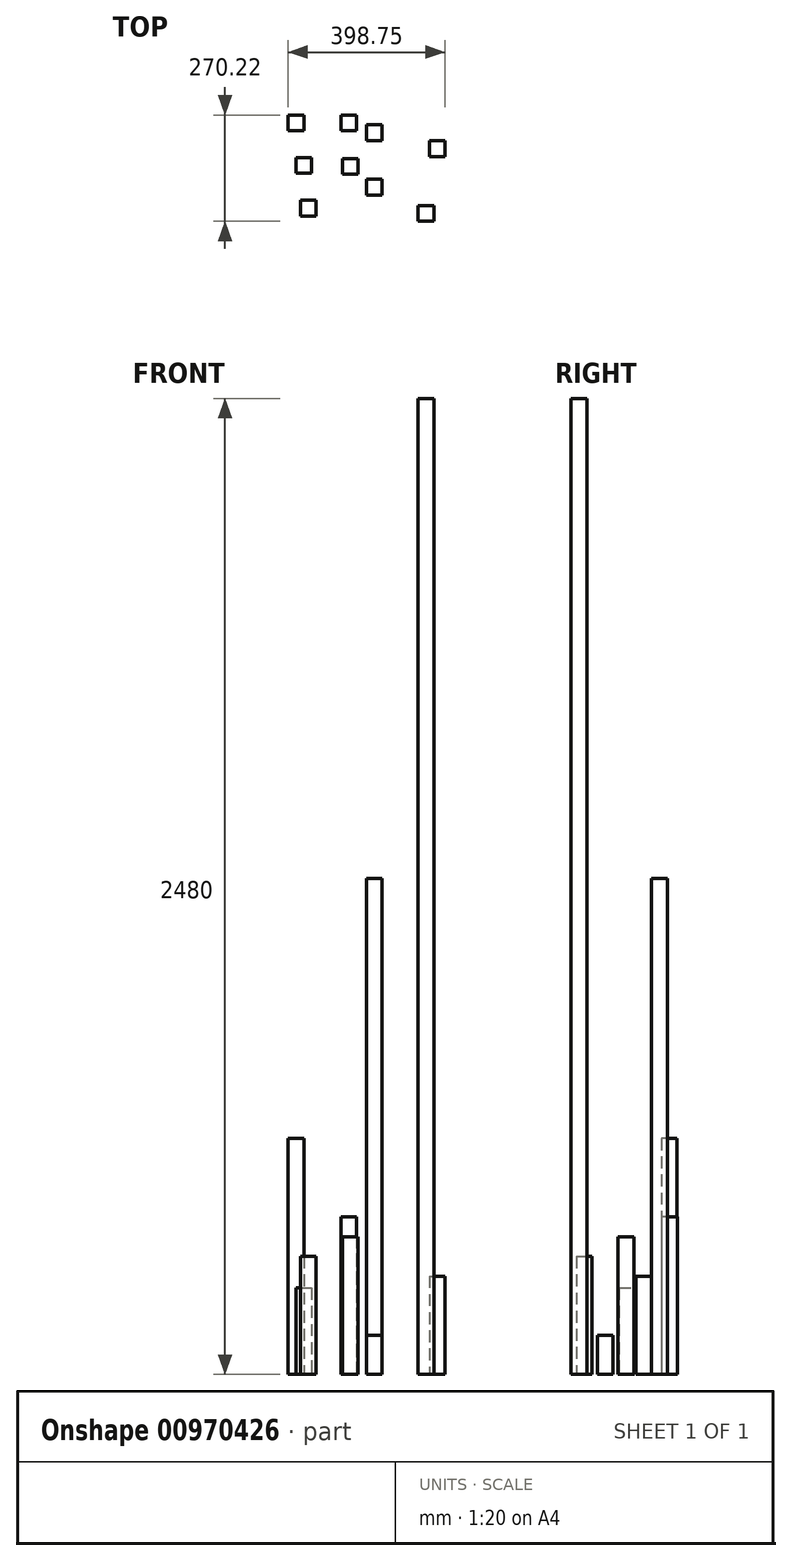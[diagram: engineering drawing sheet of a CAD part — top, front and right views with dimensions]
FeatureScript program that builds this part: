
annotation { "Feature Type Name" : "Feature", "Feature Type Description" : "" }
export const myFeature = defineFeature(function(context is Context, id is Id, definition is map)
    precondition{}
    {
        {
            var Q0;
            Q0=qCreatedBy(makeId("Top.planeOp"),FACE);
            var sketch = newSketch(context, id + "F0", { "sketchPlane" : qUnion([Q0])});
            skLineSegment(sketch, "E0.bottom", {"start": v(0, 0) * mm, "end": v(40, 0) * mm});
            skLineSegment(sketch, "E0.top", {"start": v(0, 40) * mm, "end": v(40, 40) * mm});
            skLineSegment(sketch, "E0.left", {"start": v(0, 0) * mm, "end": v(0, 40) * mm});
            skLineSegment(sketch, "E0.right", {"start": v(40, 0) * mm, "end": v(40, 40) * mm});
            skSolve(sketch);
        }
        {
            var Q0;
            Q0 = qSketchRegion(id + "F0", true);
            extrude(context, id + "F1", {"entities" : qUnion([Q0]), "depth" : 1260 * mm, "offsetDistance" : 25 * mm});
        }
        {
            var Q0;
            Q0=qCreatedBy(makeId("Top.planeOp"),FACE);
            var sketch = newSketch(context, id + "F2", { "sketchPlane" : qUnion([Q0])});
            skLineSegment(sketch, "E1.bottom", {"start": v(-178.75, -83.16) * mm, "end": v(-138.75, -83.16) * mm});
            skLineSegment(sketch, "E1.top", {"start": v(-178.75, -43.16) * mm, "end": v(-138.75, -43.16) * mm});
            skLineSegment(sketch, "E1.left", {"start": v(-178.75, -83.16) * mm, "end": v(-178.75, -43.16) * mm});
            skLineSegment(sketch, "E1.right", {"start": v(-138.75, -83.16) * mm, "end": v(-138.75, -43.16) * mm});
            skSolve(sketch);
        }
        {
            var Q0;
            Q0 = qSketchRegion(id + "F2", true);
            extrude(context, id + "F3", {"entities" : qUnion([Q0]), "depth" : 220 * mm, "offsetDistance" : 25 * mm});
        }
        {
            var Q0;
            Q0=qCreatedBy(makeId("Top.planeOp"),FACE);
            var sketch = newSketch(context, id + "F4", { "sketchPlane" : qUnion([Q0])});
            skLineSegment(sketch, "E2.bottom", {"start": v(159.9, -40.58) * mm, "end": v(199.9, -40.58) * mm});
            skLineSegment(sketch, "E2.top", {"start": v(159.9, -0.58) * mm, "end": v(199.9, -0.58) * mm});
            skLineSegment(sketch, "E2.left", {"start": v(159.9, -40.58) * mm, "end": v(159.9, -0.58) * mm});
            skLineSegment(sketch, "E2.right", {"start": v(199.9, -40.58) * mm, "end": v(199.9, -0.58) * mm});
            skSolve(sketch);
        }
        {
            var Q0;
            Q0=makeQuery(id+"F4.imprint","IMPRINT",FACE,{"disambiguationData":[TD([[makeQuery(id+"F4.imprint","IMPRINT",EDGE,{"derivedFrom":sQuery(id+"F4.wireOp",EDGE,"E2.bottom")}),1.0]])]});
            extrude(context, id + "F5", {"entities" : qUnion([Q0]), "depth" : 250 * mm, "offsetDistance" : 25 * mm});
        }
        {
            var Q0;
            Q0=qCreatedBy(makeId("Top.planeOp"),FACE);
            var sketch = newSketch(context, id + "F6", { "sketchPlane" : qUnion([Q0])});
            skLineSegment(sketch, "E3.bottom", {"start": v(-167.6, -191.22) * mm, "end": v(-127.6, -191.22) * mm});
            skLineSegment(sketch, "E3.top", {"start": v(-167.6, -151.22) * mm, "end": v(-127.6, -151.22) * mm});
            skLineSegment(sketch, "E3.left", {"start": v(-167.6, -191.22) * mm, "end": v(-167.6, -151.22) * mm});
            skLineSegment(sketch, "E3.right", {"start": v(-127.6, -191.22) * mm, "end": v(-127.6, -151.22) * mm});
            skSolve(sketch);
        }
        {
            var Q0;
            Q0 = qSketchRegion(id + "F6", true);
            extrude(context, id + "F7", {"entities" : qUnion([Q0]), "depth" : 300 * mm, "offsetDistance" : 25 * mm});
        }
        {
            var Q0;
            Q0=qCreatedBy(makeId("Top.planeOp"),FACE);
            var sketch = newSketch(context, id + "F8", { "sketchPlane" : qUnion([Q0])});
            skLineSegment(sketch, "E4.bottom", {"start": v(131.45, -205) * mm, "end": v(171.45, -205) * mm});
            skLineSegment(sketch, "E4.top", {"start": v(131.45, -165) * mm, "end": v(171.45, -165) * mm});
            skLineSegment(sketch, "E4.left", {"start": v(131.45, -205) * mm, "end": v(131.45, -165) * mm});
            skLineSegment(sketch, "E4.right", {"start": v(171.45, -205) * mm, "end": v(171.45, -165) * mm});
            skSolve(sketch);
        }
        {
            var Q0;
            Q0=makeQuery(id+"F8.imprint","IMPRINT",FACE,{"disambiguationData":[TD([[makeQuery(id+"F8.imprint","IMPRINT",EDGE,{"derivedFrom":sQuery(id+"F8.wireOp",EDGE,"E4.bottom")}),1.0]])]});
            extrude(context, id + "F9", {"entities" : qUnion([Q0]), "depth" : 2480 * mm, "offsetDistance" : 25 * mm});
        }
        {
            var Q0;
            Q0=qCreatedBy(makeId("Top.planeOp"),FACE);
            var sketch = newSketch(context, id + "F10", { "sketchPlane" : qUnion([Q0])});
            skLineSegment(sketch, "E5.bottom", {"start": v(-198.85, 64.83) * mm, "end": v(-158.85, 64.83) * mm});
            skLineSegment(sketch, "E5.top", {"start": v(-198.85, 24.83) * mm, "end": v(-158.85, 24.83) * mm});
            skLineSegment(sketch, "E5.left", {"start": v(-198.85, 64.83) * mm, "end": v(-198.85, 24.83) * mm});
            skLineSegment(sketch, "E5.right", {"start": v(-158.85, 64.83) * mm, "end": v(-158.85, 24.83) * mm});
            skSolve(sketch);
        }
        {
            var Q0;
            Q0=makeQuery(id+"F10.imprint","IMPRINT",FACE,{"disambiguationData":[TD([[makeQuery(id+"F10.imprint","IMPRINT",EDGE,{"derivedFrom":sQuery(id+"F10.wireOp",EDGE,"E5.bottom")}),-1.0]])]});
            extrude(context, id + "F11", {"entities" : qUnion([Q0]), "depth" : 600 * mm, "offsetDistance" : 25 * mm});
        }
        {
            var Q0;
            Q0=qCreatedBy(makeId("Top.planeOp"),FACE);
            var sketch = newSketch(context, id + "F12", { "sketchPlane" : qUnion([Q0])});
            skLineSegment(sketch, "E6.bottom", {"start": v(-64.52, 65.22) * mm, "end": v(-24.52, 65.22) * mm});
            skLineSegment(sketch, "E6.top", {"start": v(-64.52, 25.22) * mm, "end": v(-24.52, 25.22) * mm});
            skLineSegment(sketch, "E6.left", {"start": v(-64.52, 65.22) * mm, "end": v(-64.52, 25.22) * mm});
            skLineSegment(sketch, "E6.right", {"start": v(-24.52, 65.22) * mm, "end": v(-24.52, 25.22) * mm});
            skSolve(sketch);
        }
        {
            var Q0;
            Q0=makeQuery(id+"F12.imprint","IMPRINT",FACE,{"disambiguationData":[TD([[makeQuery(id+"F12.imprint","IMPRINT",EDGE,{"derivedFrom":sQuery(id+"F12.wireOp",EDGE,"E6.bottom")}),-1.0]])]});
            extrude(context, id + "F13", {"entities" : qUnion([Q0]), "depth" : 400 * mm, "offsetDistance" : 25 * mm});
        }
        {
            var Q0;
            Q0=qCreatedBy(makeId("Top.planeOp"),FACE);
            var sketch = newSketch(context, id + "F14", { "sketchPlane" : qUnion([Q0])});
            skLineSegment(sketch, "E7.bottom", {"start": v(0, -98.2) * mm, "end": v(40, -98.2) * mm});
            skLineSegment(sketch, "E7.top", {"start": v(0, -138.2) * mm, "end": v(40, -138.2) * mm});
            skLineSegment(sketch, "E7.left", {"start": v(0, -98.2) * mm, "end": v(0, -138.2) * mm});
            skLineSegment(sketch, "E7.right", {"start": v(40, -98.2) * mm, "end": v(40, -138.2) * mm});
            skSolve(sketch);
        }
        {
            var Q0;
            Q0=makeQuery(id+"F14.imprint","IMPRINT",FACE,{"disambiguationData":[TD([[makeQuery(id+"F14.imprint","IMPRINT",EDGE,{"derivedFrom":sQuery(id+"F14.wireOp",EDGE,"E7.bottom")}),-1.0]])]});
            extrude(context, id + "F15", {"entities" : qUnion([Q0]), "depth" : 100 * mm, "offsetDistance" : 25 * mm});
        }
        {
            var Q0;
            Q0=qCreatedBy(makeId("Top.planeOp"),FACE);
            var sketch = newSketch(context, id + "F16", { "sketchPlane" : qUnion([Q0])});
            skLineSegment(sketch, "E8.bottom", {"start": v(-60.64, -45.35) * mm, "end": v(-20.64, -45.35) * mm});
            skLineSegment(sketch, "E8.top", {"start": v(-60.64, -85.35) * mm, "end": v(-20.64, -85.35) * mm});
            skLineSegment(sketch, "E8.left", {"start": v(-60.64, -45.35) * mm, "end": v(-60.64, -85.35) * mm});
            skLineSegment(sketch, "E8.right", {"start": v(-20.64, -45.35) * mm, "end": v(-20.64, -85.35) * mm});
            skSolve(sketch);
        }
        {
            var Q0;
            Q0=makeQuery(id+"F16.imprint","IMPRINT",FACE,{"disambiguationData":[TD([[makeQuery(id+"F16.imprint","IMPRINT",EDGE,{"derivedFrom":sQuery(id+"F16.wireOp",EDGE,"E8.bottom")}),-1.0]])]});
            extrude(context, id + "F17", {"entities" : qUnion([Q0]), "depth" : 350 * mm, "offsetDistance" : 25 * mm});
        }
    });
